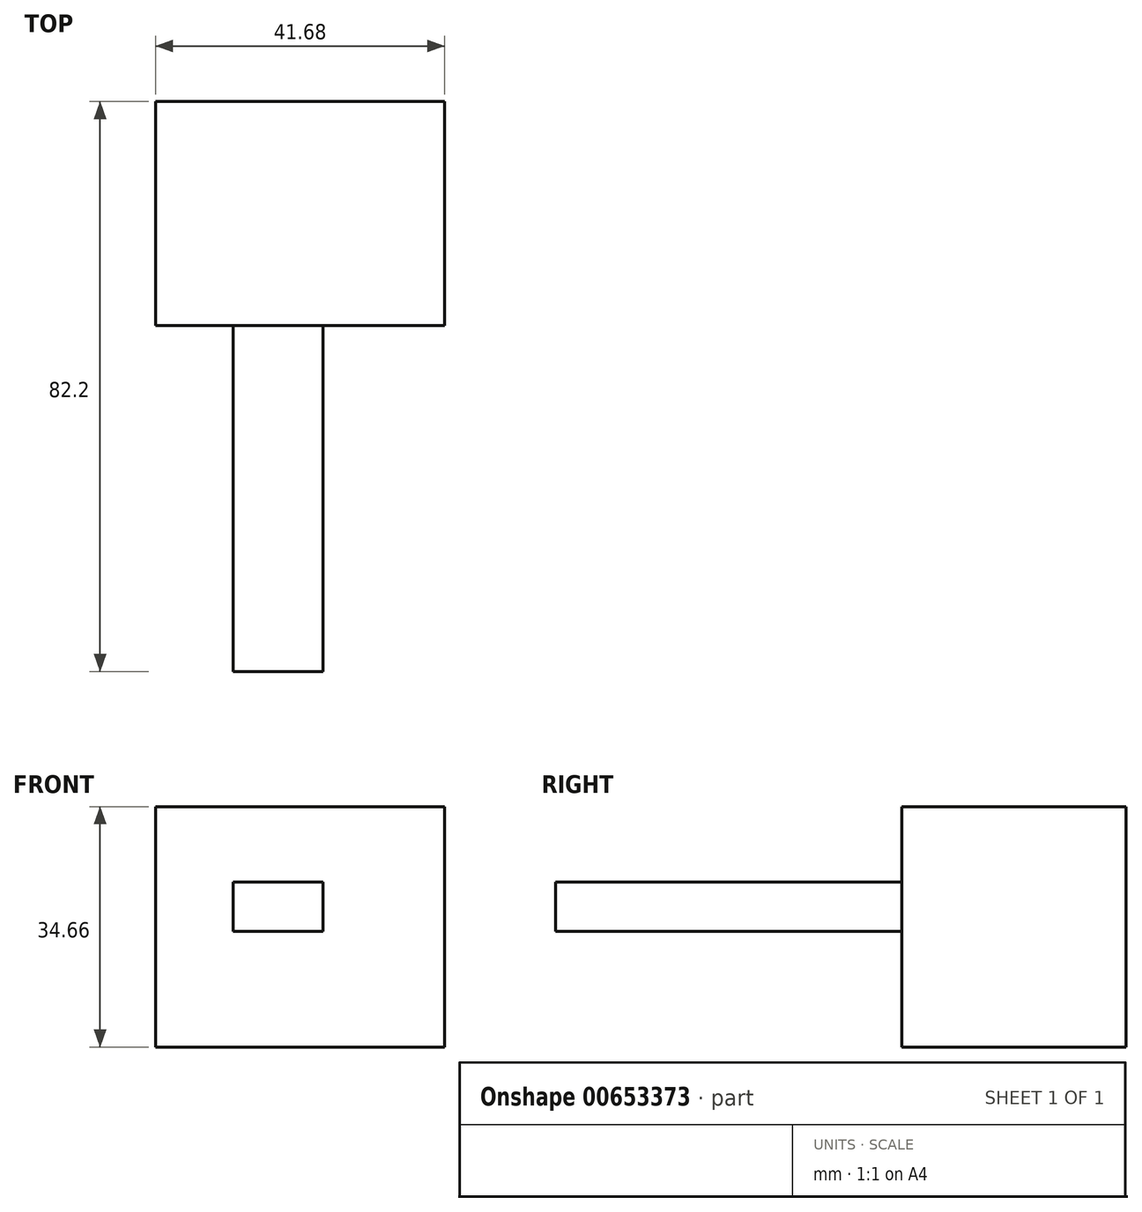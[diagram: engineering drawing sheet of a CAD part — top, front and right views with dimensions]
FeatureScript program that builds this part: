
annotation { "Feature Type Name" : "Feature", "Feature Type Description" : "" }
export const myFeature = defineFeature(function(context is Context, id is Id, definition is map)
    precondition{}
    {
        {
            var Q0;
            Q0=qCreatedBy(makeId("Top.planeOp"),FACE);
            var sketch = newSketch(context, id + "F0", { "sketchPlane" : qUnion([Q0])});
            skLineSegment(sketch, "E0.bottom", {"start": v(0, 7.04) * mm, "end": v(41.68, 7.04) * mm});
            skLineSegment(sketch, "E0.top", {"start": v(0, 39.34) * mm, "end": v(41.68, 39.34) * mm});
            skLineSegment(sketch, "E0.left", {"start": v(0, 7.04) * mm, "end": v(0, 39.34) * mm});
            skLineSegment(sketch, "E0.right", {"start": v(41.68, 7.04) * mm, "end": v(41.68, 39.34) * mm});
            skSolve(sketch);
        }
        {
            var Q0;
            Q0=makeQuery(id+"F0.imprint","IMPRINT",FACE,{"disambiguationData":[TD([[makeQuery(id+"F0.imprint","IMPRINT",EDGE,{"derivedFrom":sQuery(id+"F0.wireOp",EDGE,"E0.bottom")}),1.0]])]});
            extrude(context, id + "F1", {"entities" : qUnion([Q0]), "depth" : 34.66 * mm, "offsetDistance" : 25.4 * mm});
        }
        {
            var Q0;
            Q0=makeQuery(id+"F1.opExtrude","SWEPT_FACE",FACE,{"disambiguationData":[OSD([sQuery(id+"F0.wireOp",EDGE,"E0.top")])]});
            var sketch = newSketch(context, id + "F2", { "sketchPlane" : qUnion([Q0])});
            skLineSegment(sketch, "E1.bottom", {"start": v(-24.14, 16.68) * mm, "end": v(-11.22, 16.68) * mm});
            skLineSegment(sketch, "E1.top", {"start": v(-24.14, 23.81) * mm, "end": v(-11.22, 23.81) * mm});
            skLineSegment(sketch, "E1.left", {"start": v(-24.14, 16.68) * mm, "end": v(-24.14, 23.81) * mm});
            skLineSegment(sketch, "E1.right", {"start": v(-11.22, 16.68) * mm, "end": v(-11.22, 23.81) * mm});
            skSolve(sketch);
        }
        {
            var Q0;
            Q0 = qSketchRegion(id + "F2", true);
            extrude(context, id + "F3", {"entities" : qUnion([Q0]), "operationType" : NewBodyOperationType.ADD, "oppositeDirection" : true, "depth" : 82.2 * mm, "offsetDistance" : 25.4 * mm});
        }
    });
